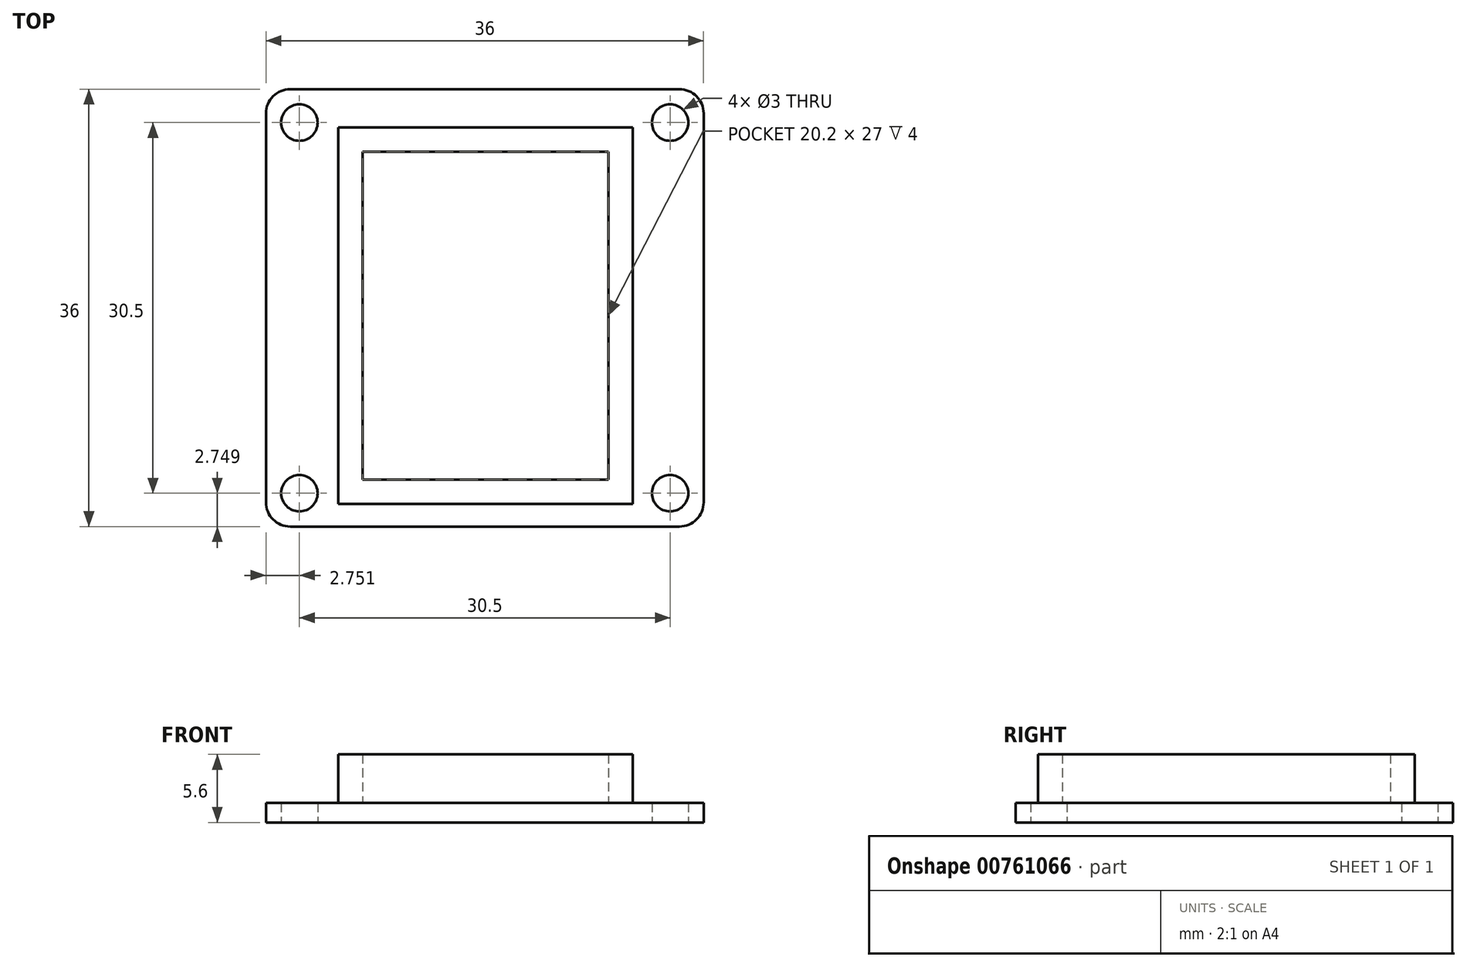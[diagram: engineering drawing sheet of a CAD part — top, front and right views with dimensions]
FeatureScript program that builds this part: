
annotation { "Feature Type Name" : "Feature", "Feature Type Description" : "" }
export const myFeature = defineFeature(function(context is Context, id is Id, definition is map)
    precondition{}
    {
        {
            var Q0;
            Q0=qCreatedBy(makeId("Top.planeOp"),FACE);
            var sketch = newSketch(context, id + "F0", { "sketchPlane" : qUnion([Q0])});
            skLineSegment(sketch, "E0.left", {"start": v(-18, 20.95) * mm, "end": v(-18, -11.05) * mm});
            skPoint(sketch, "E1.visualSharp", {"position": v(-18, 22.95) * mm});
            skPoint(sketch, "E2", {"position": v(-15.25, 20.2) * mm});
            skCircle(sketch, "E3", {"center": v(-15.25, 20.2) * mm, "radius": 1.5 * mm});
            skPoint(sketch, "E4", {"position": v(15.25, 20.2) * mm});
            skCircle(sketch, "E5", {"center": v(15.25, 20.2) * mm, "radius": 1.5 * mm});
            skPoint(sketch, "E6", {"position": v(15.25, -10.3) * mm});
            skPoint(sketch, "E7", {"position": v(-15.25, -10.3) * mm});
            skCircle(sketch, "E8", {"center": v(15.25, -10.3) * mm, "radius": 1.5 * mm});
            skCircle(sketch, "E9", {"center": v(-15.25, -10.3) * mm, "radius": 1.5 * mm});
            skArc(sketch, "E10.filletArc", {"start": v(-16, 22.95) * mm, "mid": v(-17.41, 22.36) * mm, "end": v(-18, 20.95) * mm});
            skLineSegment(sketch, "E11", {"start": v(-16, -13.05) * mm, "end": v(16, -13.05) * mm});
            skLineSegment(sketch, "E12", {"start": v(-16, 22.95) * mm, "end": v(16, 22.95) * mm});
            skLineSegment(sketch, "E13", {"start": v(18, 20.95) * mm, "end": v(18, -11.05) * mm});
            skPoint(sketch, "E14.visualSharp", {"position": v(18, 22.95) * mm});
            skArc(sketch, "E14.filletArc", {"start": v(18, 20.95) * mm, "mid": v(17.42, 22.36) * mm, "end": v(16, 22.95) * mm});
            skPoint(sketch, "E15.visualSharp", {"position": v(18, -13.05) * mm});
            skArc(sketch, "E15.filletArc", {"start": v(16, -13.05) * mm, "mid": v(17.42, -12.46) * mm, "end": v(18, -11.05) * mm});
            skPoint(sketch, "E16.visualSharp", {"position": v(-18, -13.05) * mm});
            skArc(sketch, "E16.filletArc", {"start": v(-18, -11.05) * mm, "mid": v(-17.41, -12.46) * mm, "end": v(-16, -13.05) * mm});
            skSolve(sketch);
        }
        {
            var Q0;
            Q0=makeQuery(id+"F0.imprint","IMPRINT",FACE,{"disambiguationData":[TD([[makeQuery(id+"F0.imprint","IMPRINT",EDGE,{"derivedFrom":sQuery(id+"F0.wireOp",EDGE,"E0.left")}),1.0]])]});
            extrude(context, id + "F1", {"entities" : qUnion([Q0]), "depth" : 1.6 * mm, "offsetDistance" : 25 * mm});
        }
        {
            var Q0;
            Q0=makeQuery(id+"F1.opExtrude","CAP_FACE",FACE,{"disambiguationData":[OSD([sQuery(id+"F0.wireOp",EDGE,"E0.left"),sQuery(id+"F0.wireOp",EDGE,"E3"),sQuery(id+"F0.wireOp",EDGE,"E5"),sQuery(id+"F0.wireOp",EDGE,"E8"),sQuery(id+"F0.wireOp",EDGE,"E9"),sQuery(id+"F0.wireOp",EDGE,"E10.filletArc"),sQuery(id+"F0.wireOp",EDGE,"E11"),sQuery(id+"F0.wireOp",EDGE,"E12"),sQuery(id+"F0.wireOp",EDGE,"E13"),sQuery(id+"F0.wireOp",EDGE,"E14.filletArc"),sQuery(id+"F0.wireOp",EDGE,"E15.filletArc"),sQuery(id+"F0.wireOp",EDGE,"E16.filletArc")])],"isStart":false});
            var sketch = newSketch(context, id + "F2", { "sketchPlane" : qUnion([Q0])});
            skLineSegment(sketch, "E17.bottom", {"start": v(-10.04, 17.8) * mm, "end": v(10.16, 17.8) * mm});
            skLineSegment(sketch, "E17.top", {"start": v(-10.04, -9.2) * mm, "end": v(10.16, -9.2) * mm});
            skLineSegment(sketch, "E17.left", {"start": v(-10.04, 17.8) * mm, "end": v(-10.04, -9.2) * mm});
            skLineSegment(sketch, "E17.right", {"start": v(10.16, 17.8) * mm, "end": v(10.16, -9.2) * mm});
            skLineSegment(sketch, "E18", {"start": v(12.16, -11.2) * mm, "end": v(-12.04, -11.2) * mm});
            skLineSegment(sketch, "E19", {"start": v(-12.04, 19.8) * mm, "end": v(-12.04, -11.2) * mm});
            skLineSegment(sketch, "E20", {"start": v(-12.04, 19.8) * mm, "end": v(12.16, 19.8) * mm});
            skLineSegment(sketch, "E21", {"start": v(12.16, -11.2) * mm, "end": v(12.16, 19.8) * mm});
            skSolve(sketch);
        }
        {
            var Q0;
            Q0=makeQuery(id+"F2.imprint","IMPRINT",FACE,{"disambiguationData":[TD([[makeQuery(id+"F2.imprint","IMPRINT",EDGE,{"derivedFrom":sQuery(id+"F2.wireOp",EDGE,"E17.bottom")}),1.0]])]});
            extrude(context, id + "F3", {"entities" : qUnion([Q0]), "operationType" : NewBodyOperationType.ADD, "depth" : 4 * mm, "offsetDistance" : 25 * mm});
        }
    });
